# Revit family: HeartFelt-Linear-Panel Splice1_HunterDouglasEurope
name_source: partatom
category: Specialty Equipment
revit_build: Autodesk Revit 2016 (Build: 20150220_1215(x64)
units: mm (PartAtom-declared; Revit-internal decimal feet)

## family parameters
Always vertical = Yes
Cut with Voids When Loaded = No
OmniClass Number = 23.35.70.24.11.17.14
OmniClass Title = Linear Ceilings
Part Type = Normal
Room Calculation Point = No
Round Connector Dimension = Use Diameter
Shared = No
Work Plane-Based = No

## types (3) — shared parameters
Alloy = EN AW 5050
Colour Code = 7178
EN13501-1_Fire rating = Class A2,s1,d0
Length = 220 mm  [stored 0.721785 ft]
Manufacturer = Hunter Douglas
Material = Aluminum-7178_HunterDouglasEurope
Product Data = http://assets2.hunterdouglascontract.com
Product Line = HeartFelt® Linear
Subcategory = HeartFelt® Ceilings
Thickness = 0.5 mm  [stored 0.00164042 ft]
URL = http://www.hunterdouglasarchitectural.eu

## per-type parameters (varying)
| type | Article Code | Height | Model |
| Panel Splice1_40x55 | 38.4201 | 51.5 mm  [stored 0.168963 ft] | HeartFelt Panel Splice1 40x55 |
| Panel Splice1_40x80 | 38.4202 | 76.5 mm | HeartFelt Panel Splice1 40x80 |
| Panel Splice1_40x105 | 38.4203 | 101.5 mm | HeartFelt Panel Splice1 40x105 |

note: [stored X ft] marks values corroborated as IEEE doubles in the binary element streams (Revit-internal decimal feet)

## geometry (parser evidence)
native form markers: Sweep x2
no freeform markers — native parametric forms only
